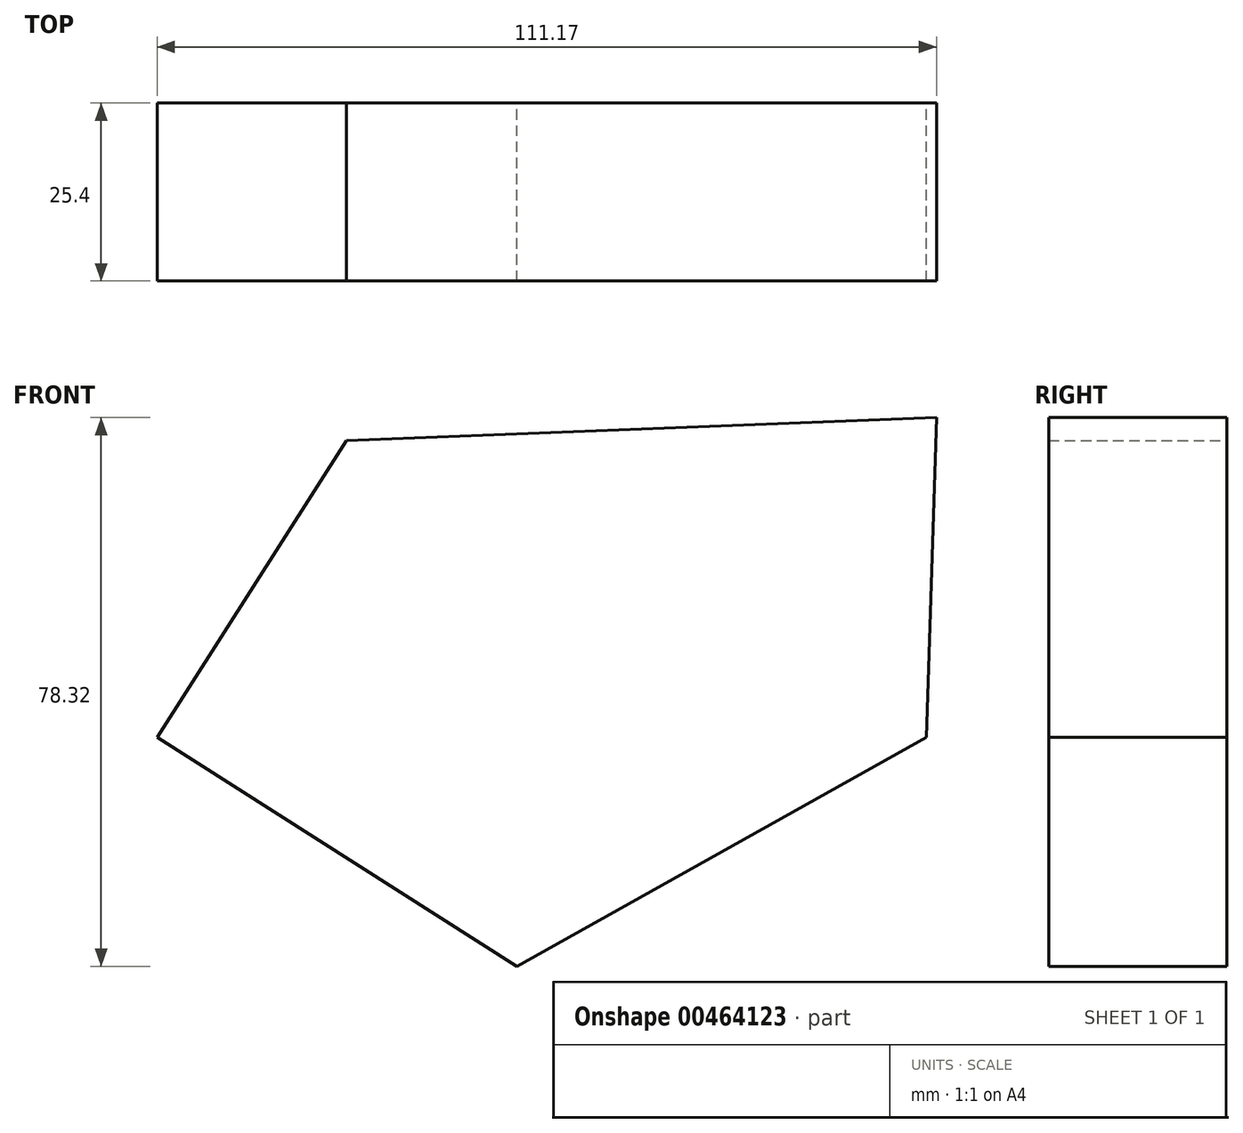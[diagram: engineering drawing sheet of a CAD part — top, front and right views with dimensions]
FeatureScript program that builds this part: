
annotation { "Feature Type Name" : "Feature", "Feature Type Description" : "" }
export const myFeature = defineFeature(function(context is Context, id is Id, definition is map)
    precondition{}
    {
        {
            var Q0;
            Q0=qCreatedBy(makeId("Front.planeOp"),FACE);
            var sketch = newSketch(context, id + "F0", { "sketchPlane" : qUnion([Q0])});
            skLineSegment(sketch, "E0", {"start": v(-24.35, 42.32) * mm, "end": v(-51.31, 0) * mm});
            skLineSegment(sketch, "E1", {"start": v(-51.31, 0) * mm, "end": v(0, -32.7) * mm});
            skLineSegment(sketch, "E2", {"start": v(0, -32.7) * mm, "end": v(58.4, 0) * mm});
            skLineSegment(sketch, "E3", {"start": v(58.4, 0) * mm, "end": v(59.86, 45.62) * mm});
            skLineSegment(sketch, "E4", {"start": v(59.86, 45.62) * mm, "end": v(-24.35, 42.32) * mm});
            skSolve(sketch);
        }
        {
            var Q0;
            Q0=makeQuery(id+"F0.imprint","IMPRINT",FACE,{"disambiguationData":[TD([[makeQuery(id+"F0.imprint","IMPRINT",EDGE,{"derivedFrom":sQuery(id+"F0.wireOp",EDGE,"E0")}),1.0]])]});
            extrude(context, id + "F1", {"entities" : qUnion([Q0]), "depth" : 25.4 * mm});
        }
    });
